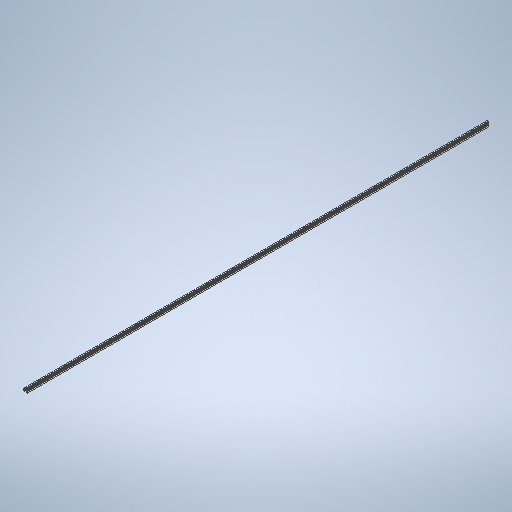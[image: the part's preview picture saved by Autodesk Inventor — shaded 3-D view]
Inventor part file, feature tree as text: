
AUTODESK INVENTOR PART (.ipt)
format: ipt  version: 2025.2 (Build 292293000, 293)  size: 351,744 bytes
history: native  units: mm
features: other x1, extrude x1, sketch x1
ambient origin geometry x8: Origin, YZ Plane, XZ Plane, XY Plane, X Axis, Y Axis, Z Axis, Center Point
bodies: Body1 (feature_tree)
feature tree (3):
  other  "Sólido1"
  extrude  "Extrusão1"  Depth=0.5mm
  sketch  "Esboço2"  dims[d6=5.0mm d7=20.0mm d8=10.0mm d9=6.2mm d11=6.0mm d17=2.0mm d22=0.5mm d24=0.5mm d65=1.5mm d67=1.5mm d69=1.5mm d70=1.5mm d72=1.5mm d75=2000.0mm d76=0.0mm d25=0.872665mm d26=0.5mm d27=0.872665mm]
